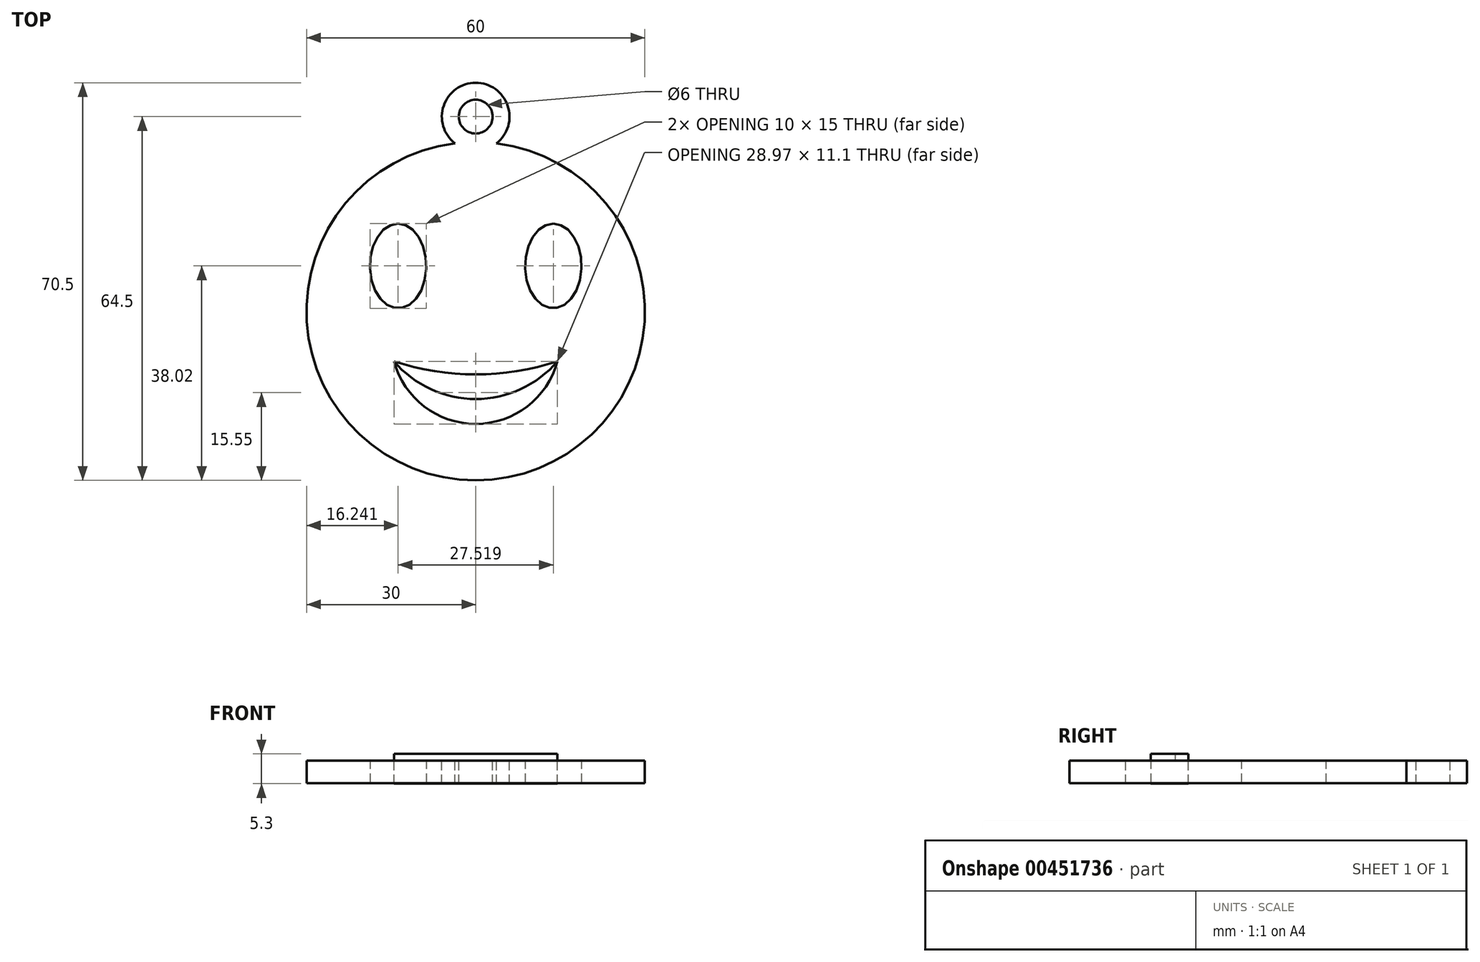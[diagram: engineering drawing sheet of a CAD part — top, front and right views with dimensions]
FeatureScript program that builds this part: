
annotation { "Feature Type Name" : "Feature", "Feature Type Description" : "" }
export const myFeature = defineFeature(function(context is Context, id is Id, definition is map)
    precondition{}
    {
        {
            var Q0;
            Q0=qCreatedBy(makeId("Top.planeOp"),FACE);
            var sketch = newSketch(context, id + "F0", { "sketchPlane" : qUnion([Q0])});
            skCircle(sketch, "E0", {"center": v(0, 0) * mm, "radius": 30 * mm});
            skEllipse(sketch, "E1", {"center": v(-13.76, 8.02) * mm, "majorRadius": 7.5 * mm, "minorRadius": 5 * mm, "majorAxis": v(0, 1)});
            skEllipse(sketch, "E2.MirrorC", {"center": v(13.76, 8.02) * mm, "majorRadius": 7.5 * mm, "minorRadius": 5 * mm, "majorAxis": v(0, 1)});
            skArc(sketch, "E3", {"start": v(-18.88, -15.22) * mm, "mid": v(-0.26, -23.8) * mm, "end": v(18.51, -15.56) * mm});
            skArc(sketch, "E4.0", {"start": v(-14.42, -12.7) * mm, "mid": v(-0.35, -18.8) * mm, "end": v(13.9, -13.15) * mm});
            skLineSegment(sketch, "E5", {"start": v(13.9, -13.15) * mm, "end": v(18.51, -15.56) * mm});
            skLineSegment(sketch, "E6", {"start": v(-14.42, -12.7) * mm, "end": v(-18.88, -15.22) * mm});
            skArc(sketch, "E7", {"start": v(-16.65, -13.96) * mm, "mid": v(-0.3, -21.17) * mm, "end": v(16.2, -14.35) * mm});
            skSolve(sketch);
        }
        {
            var Q0;
            Q0=makeQuery(id+"F0.imprint","IMPRINT",FACE,{"disambiguationData":[TD([[makeQuery(id+"F0.imprint","IMPRINT",EDGE,{"derivedFrom":sQuery(id+"F0.wireOp",EDGE,"uCWqCDSW-LE0Y-BLAe-JTsF-9iLlV4xVZKp5")}),1.0]])]});
            var Q1;
            Q1=makeQuery(id+"F0.imprint","IMPRINT",FACE,{"disambiguationData":[TD([[makeQuery(id+"F0.imprint","IMPRINT",EDGE,{"derivedFrom":sQuery(id+"F0.wireOp",EDGE,"E0")}),1.0]])]});
            var Q2;
            Q2=makeQuery(id+"F0.imprint","IMPRINT",FACE,{"disambiguationData":[TD([[makeQuery(id+"F0.imprint","IMPRINT",EDGE,{"derivedFrom":sQuery(id+"F0.wireOp",EDGE,"E2.MirrorC")}),1.0]])]});
            var Q3;
            Q3=makeQuery(id+"F0.imprint","IMPRINT",FACE,{"disambiguationData":[TD([[makeQuery(id+"F0.imprint","IMPRINT",EDGE,{"derivedFrom":sQuery(id+"F0.wireOp",EDGE,"E1")}),1.0]])]});
            var Q4;
            {var subQ0=sQuery(id+"F0.wireOp",EDGE,"E4.0");Q4=makeQuery(id+"F0.imprint","IMPRINT",FACE,{"disambiguationData":[TD([[makeQuery(id+"F0.imprint","IMPRINT",EDGE,{"derivedFrom":subQ0}),-1.0]])]});}
            var Q5;
            {var subQ0=sQuery(id+"F0.wireOp",EDGE,"E3");Q5=makeQuery(id+"F0.imprint","IMPRINT",FACE,{"disambiguationData":[TD([[makeQuery(id+"F0.imprint","IMPRINT",EDGE,{"derivedFrom":subQ0}),1.0]])]});}
            var Q6;
            Q6=sQuery(id+"F0.wireOp",EDGE,"uCWqCDSW-LE0Y-BLAe-JTsF-9iLlV4xVZKp5");
            extrude(context, id + "F1", {"entities" : qUnion([Q0, Q1, Q2, Q3, Q4, Q5]), "surfaceEntities" : qUnion([Q6]), "depth" : 4 * mm});
        }
        {
            var Q0;
            Q0=makeQuery(id+"F1.opExtrude","CAP_FACE",FACE,{"disambiguationData":[OSD([sQuery(id+"F0.wireOp",EDGE,"E0")])],"isStart":false});
            var sketch = newSketch(context, id + "F2", { "sketchPlane" : qUnion([Q0])});
            skArc(sketch, "E8", {"start": v(-14.48, -8.9) * mm, "mid": v(0, -20) * mm, "end": v(14.48, -8.9) * mm});
            skArc(sketch, "E9", {"start": v(-14.48, -8.9) * mm, "mid": v(0, -11.21) * mm, "end": v(14.48, -8.9) * mm});
            skSolve(sketch);
        }
        {
            var Q0;
            Q0=makeQuery(id+"F2.imprint","IMPRINT",FACE,{"disambiguationData":[TD([[makeQuery(id+"F2.imprint","IMPRINT",EDGE,{"derivedFrom":sQuery(id+"F2.wireOp",EDGE,"E8")}),1.0]])]});
            extrude(context, id + "F3", {"entities" : qUnion([Q0]), "operationType" : NewBodyOperationType.REMOVE, "oppositeDirection" : true, "depth" : 15.7 * mm});
        }
        {
            var Q0;
            Q0=makeQuery(id+"F1.opExtrude","CAP_FACE",FACE,{"disambiguationData":[OSD([sQuery(id+"F0.wireOp",EDGE,"E0")])],"isStart":false});
            var sketch = newSketch(context, id + "F4", { "sketchPlane" : qUnion([Q0])});
            skArc(sketch, "E10", {"start": v(-14.48, -8.9) * mm, "mid": v(0, -15.1) * mm, "end": v(14.48, -8.9) * mm});
            skSolve(sketch);
        }
        {
            var Q0;
            Q0=makeQuery(id+"F0.imprint","IMPRINT",FACE,{"disambiguationData":[TD([[makeQuery(id+"F0.imprint","IMPRINT",EDGE,{"derivedFrom":sQuery(id+"F0.wireOp",EDGE,"E1")}),1.0]])]});
            var Q1;
            Q1=makeQuery(id+"F0.imprint","IMPRINT",FACE,{"disambiguationData":[TD([[makeQuery(id+"F0.imprint","IMPRINT",EDGE,{"derivedFrom":sQuery(id+"F0.wireOp",EDGE,"E2.MirrorC")}),1.0]])]});
            extrude(context, id + "F5", {"entities" : qUnion([Q0, Q1]), "operationType" : NewBodyOperationType.REMOVE, "depth" : 14.1 * mm});
        }
        {
            var Q0;
            Q0=makeQuery(id+"F2.imprint","IMPRINT",FACE,{"disambiguationData":[TD([[makeQuery(id+"F2.imprint","IMPRINT",EDGE,{"derivedFrom":sQuery(id+"F2.wireOp",EDGE,"E8")}),-1.0]])]});
            var sketch = newSketch(context, id + "F6", { "sketchPlane" : qUnion([Q0])});
            skArc(sketch, "E11", {"start": v(-14.48, -8.9) * mm, "mid": v(0, -15.58) * mm, "end": v(14.48, -8.9) * mm});
            skArc(sketch, "E12.0", {"start": v(-14.48, -8.9) * mm, "mid": v(0, -11.21) * mm, "end": v(14.48, -8.9) * mm});
            skSolve(sketch);
        }
        {
            var Q0;
            Q0 = qSketchRegion(id + "F6", true);
            extrude(context, id + "F7", {"entities" : qUnion([Q0]), "operationType" : NewBodyOperationType.ADD, "depth" : 1.2 * mm, "hasSecondDirection" : true, "secondDirectionOppositeDirection" : true, "secondDirectionDepth" : 4.1 * mm});
        }
        {
            var Q0;
            Q0=makeQuery(id+"F2.imprint","IMPRINT",FACE,{"disambiguationData":[TD([[makeQuery(id+"F2.imprint","IMPRINT",EDGE,{"derivedFrom":sQuery(id+"F2.wireOp",EDGE,"E8")}),-1.0]])]});
            var sketch = newSketch(context, id + "F8", { "sketchPlane" : qUnion([Q0])});
            skCircle(sketch, "E13", {"center": v(0, 34.5) * mm, "radius": 6 * mm});
            skCircle(sketch, "E14", {"center": v(0, 34.5) * mm, "radius": 3 * mm});
            skSolve(sketch);
        }
        {
            var Q0;
            Q0 = qSketchRegion(id + "F8", true);
            extrude(context, id + "F9", {"entities" : qUnion([Q0]), "operationType" : NewBodyOperationType.ADD, "oppositeDirection" : true, "depth" : 4 * mm});
        }
    });
